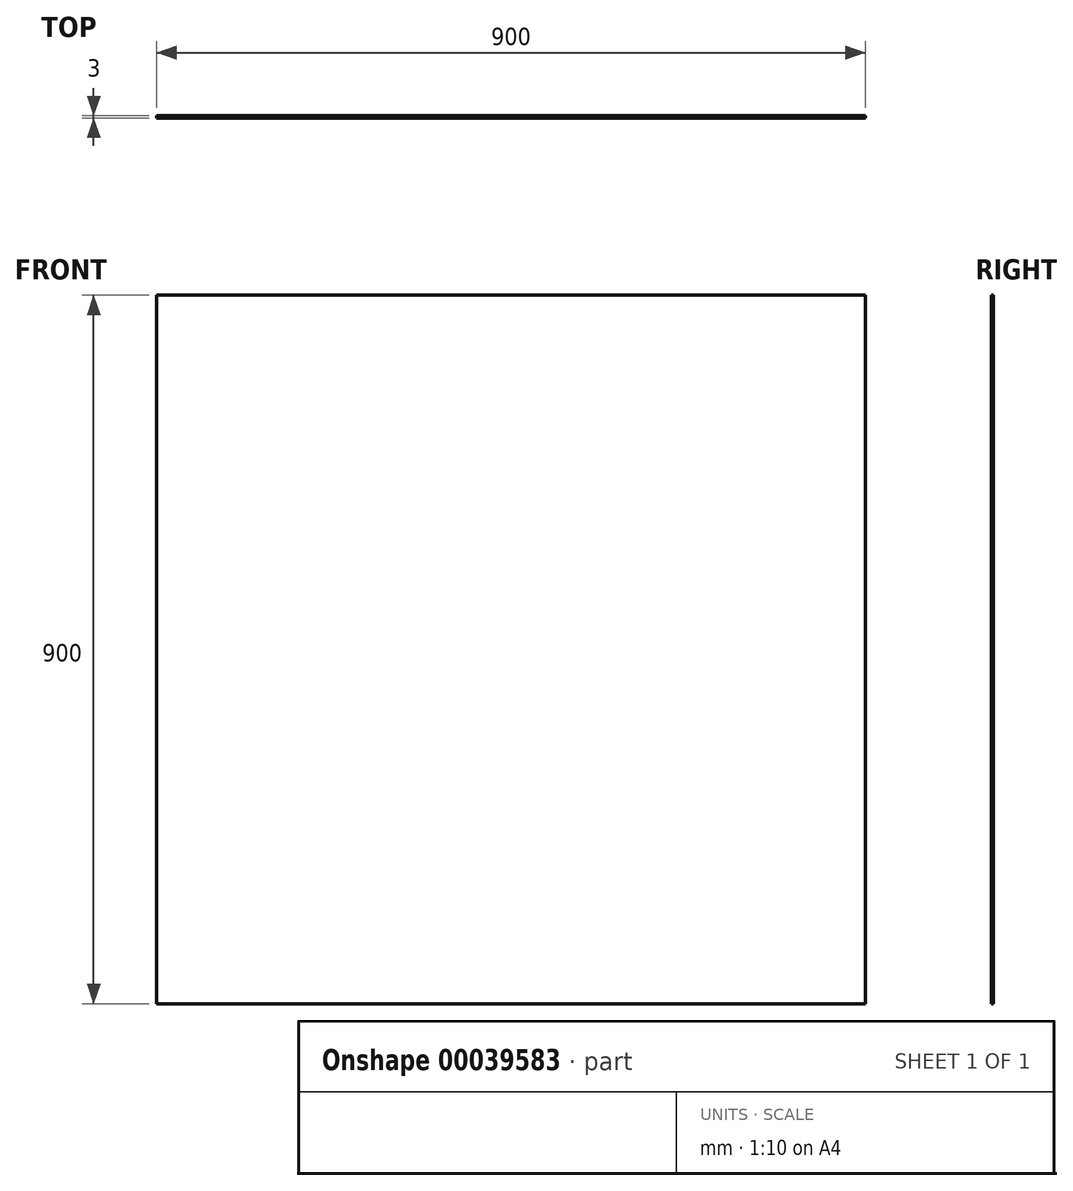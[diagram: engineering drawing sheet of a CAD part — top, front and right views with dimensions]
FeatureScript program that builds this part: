
annotation { "Feature Type Name" : "Feature", "Feature Type Description" : "" }
export const myFeature = defineFeature(function(context is Context, id is Id, definition is map)
    precondition{}
    {
        {
            var Q0;
            Q0=qCreatedBy(makeId("Front.planeOp"),FACE);
            var sketch = newSketch(context, id + "F0", { "sketchPlane" : qUnion([Q0])});
            skLineSegment(sketch, "E0.bottom", {"start": v(-1114.17, 723.11) * mm, "end": v(-214.17, 723.11) * mm});
            skLineSegment(sketch, "E0.top", {"start": v(-1114.17, -176.89) * mm, "end": v(-214.17, -176.89) * mm});
            skLineSegment(sketch, "E0.left", {"start": v(-1114.17, 723.11) * mm, "end": v(-1114.17, -176.89) * mm});
            skLineSegment(sketch, "E0.right", {"start": v(-214.17, 723.11) * mm, "end": v(-214.17, -176.89) * mm});
            skSolve(sketch);
        }
        {
            var Q0;
            Q0=makeQuery(id+"F0.imprint","IMPRINT",FACE,{"disambiguationData":[TD([[makeQuery(id+"F0.imprint","IMPRINT",EDGE,{"derivedFrom":sQuery(id+"F0.wireOp",EDGE,"E0.bottom")}),-1.0]])]});
            extrude(context, id + "F1", {"entities" : qUnion([Q0]), "depth" : 3 * mm});
        }
    });
